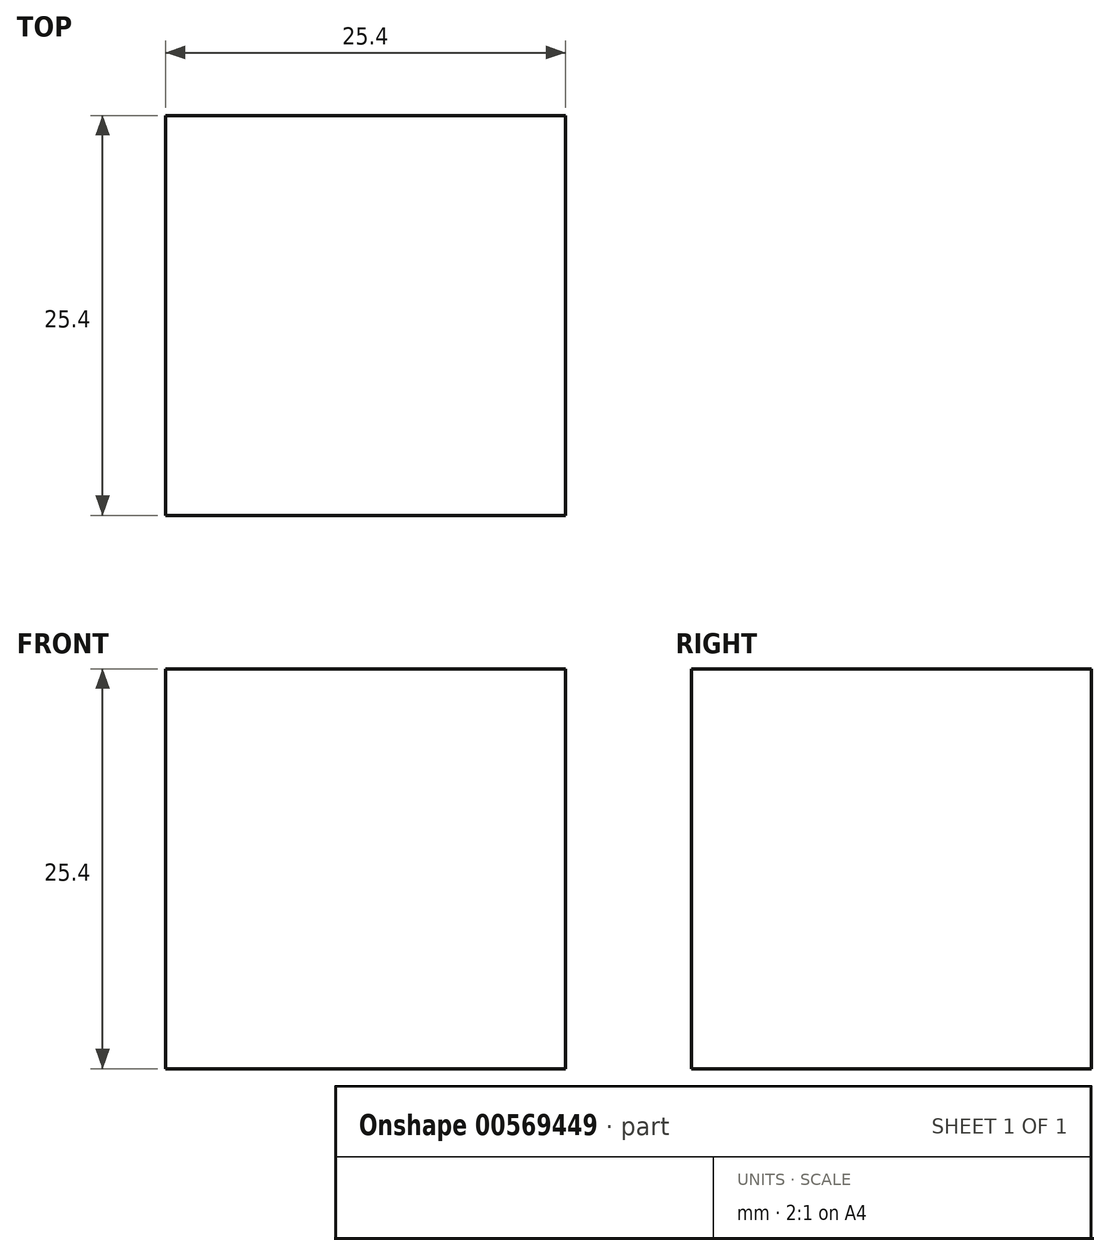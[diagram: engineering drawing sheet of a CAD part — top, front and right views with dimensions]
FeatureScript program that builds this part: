
annotation { "Feature Type Name" : "Feature", "Feature Type Description" : "" }
export const myFeature = defineFeature(function(context is Context, id is Id, definition is map)
    precondition{}
    {
        {
            var Q0;
            Q0=qCreatedBy(makeId("Front.planeOp"),FACE);
            var sketch = newSketch(context, id + "F0", { "sketchPlane" : qUnion([Q0])});
            skLineSegment(sketch, "E0.bottom", {"start": v(-25.4, 32.23) * mm, "end": v(0, 32.23) * mm});
            skLineSegment(sketch, "E0.top", {"start": v(-25.4, 6.83) * mm, "end": v(0, 6.83) * mm});
            skLineSegment(sketch, "E0.left", {"start": v(-25.4, 32.23) * mm, "end": v(-25.4, 6.83) * mm});
            skLineSegment(sketch, "E0.right", {"start": v(0, 32.23) * mm, "end": v(0, 6.83) * mm});
            skSolve(sketch);
        }
        {
            var Q0;
            Q0=makeQuery(id+"F0.imprint","IMPRINT",FACE,{"disambiguationData":[TD([[makeQuery(id+"F0.imprint","IMPRINT",EDGE,{"derivedFrom":sQuery(id+"F0.wireOp",EDGE,"E0.bottom")}),-1.0]])]});
            extrude(context, id + "F1", {"entities" : qUnion([Q0]), "depth" : 25.4 * mm, "offsetDistance" : 25.4 * mm});
        }
    });
